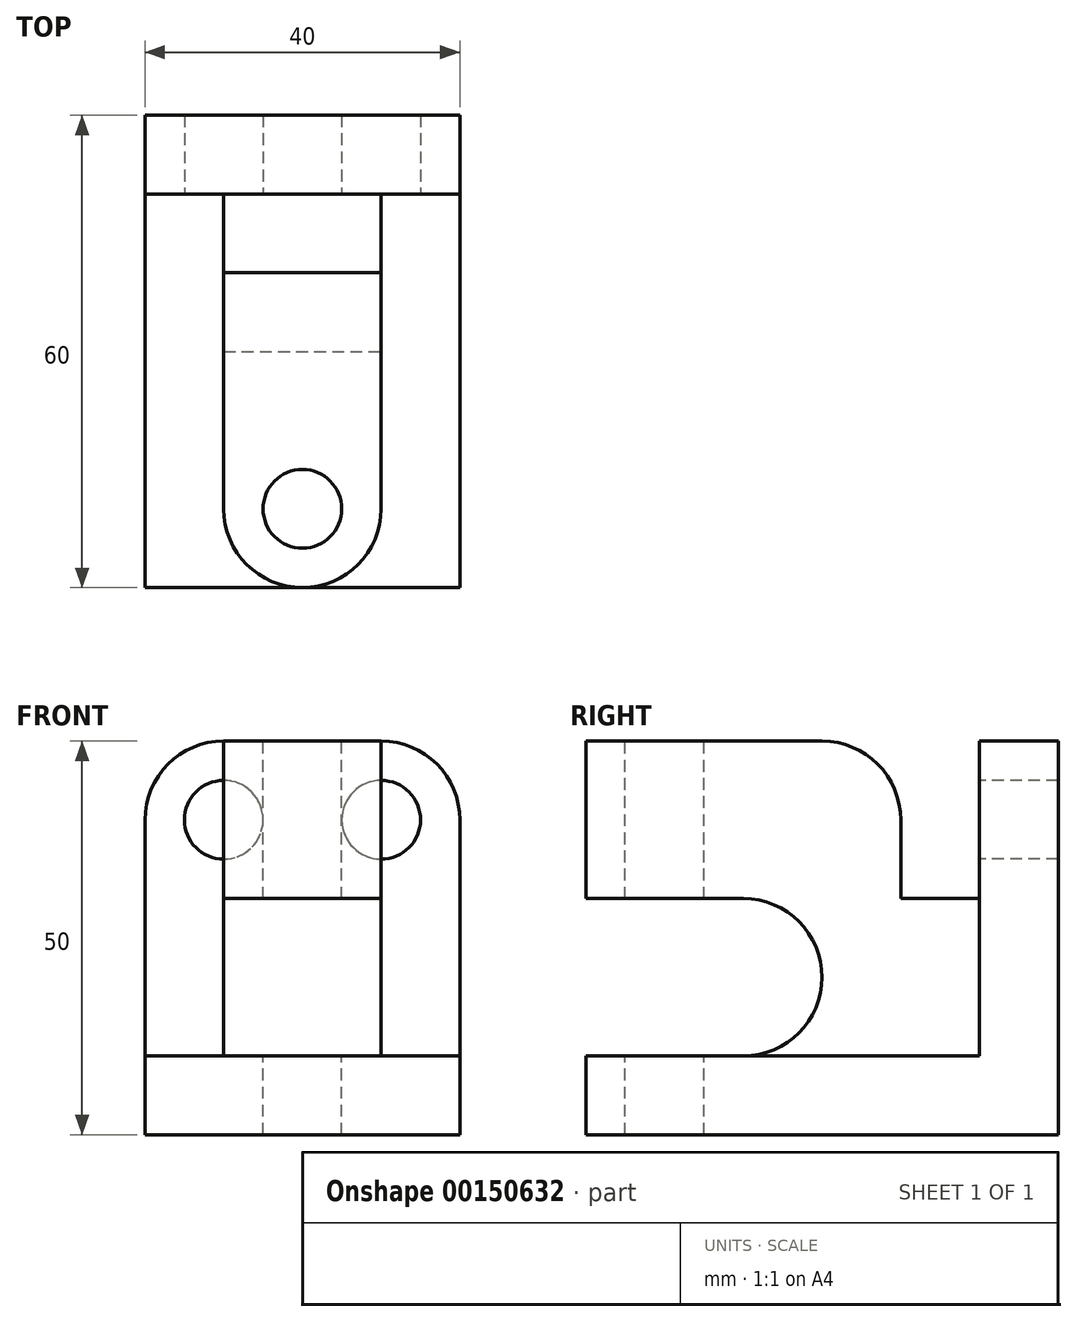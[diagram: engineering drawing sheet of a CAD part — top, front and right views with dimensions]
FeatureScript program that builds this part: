
annotation { "Feature Type Name" : "Feature", "Feature Type Description" : "" }
export const myFeature = defineFeature(function(context is Context, id is Id, definition is map)
    precondition{}
    {
        {
            var Q0;
            Q0=qCreatedBy(makeId("Right.planeOp"),FACE);
            var sketch = newSketch(context, id + "F0", { "sketchPlane" : qUnion([Q0])});
            skLineSegment(sketch, "E0", {"start": v(0, 0) * mm, "end": v(0, 50) * mm});
            skLineSegment(sketch, "E1", {"start": v(0, 50) * mm, "end": v(-10, 50) * mm});
            skLineSegment(sketch, "E2", {"start": v(-10, 50) * mm, "end": v(-10, 10) * mm});
            skLineSegment(sketch, "E3", {"start": v(-10, 10) * mm, "end": v(-60, 10) * mm});
            skLineSegment(sketch, "E4", {"start": v(-60, 10) * mm, "end": v(-60, 0) * mm});
            skLineSegment(sketch, "E5", {"start": v(-60, 0) * mm, "end": v(0, 0) * mm});
            skSolve(sketch);
        }
        {
            var Q0;
            Q0=makeQuery(id+"F0.imprint","IMPRINT",FACE,{"disambiguationData":[TD([[makeQuery(id+"F0.imprint","IMPRINT",EDGE,{"derivedFrom":sQuery(id+"F0.wireOp",EDGE,"E0")}),1.0]])]});
            extrude(context, id + "F1", {"entities" : qUnion([Q0]), "endBound" : BoundingType.SYMMETRIC, "depth" : 40 * mm});
        }
        {
            var Q0;
            Q0=qCreatedBy(makeId("Right.planeOp"),FACE);
            var sketch = newSketch(context, id + "F2", { "sketchPlane" : qUnion([Q0])});
            skLineSegment(sketch, "E6", {"start": v(-10, 10) * mm, "end": v(-60, 10) * mm});
            skLineSegment(sketch, "E7", {"start": v(-60, 10) * mm, "end": v(-60, 50) * mm});
            skLineSegment(sketch, "E8", {"start": v(-60, 50) * mm, "end": v(-30, 50) * mm});
            skLineSegment(sketch, "E9", {"start": v(-20, 40) * mm, "end": v(-20, 30) * mm});
            skLineSegment(sketch, "E10", {"start": v(-20, 30) * mm, "end": v(-10, 30) * mm});
            skLineSegment(sketch, "E11", {"start": v(-10, 30) * mm, "end": v(-10, 10) * mm});
            skPoint(sketch, "E12.visualSharp", {"position": v(-20, 50) * mm});
            skArc(sketch, "E12.filletArc", {"start": v(-20, 40) * mm, "mid": v(-22.93, 47.07) * mm, "end": v(-30, 50) * mm});
            skSolve(sketch);
        }
        {
            var Q0;
            Q0=makeQuery(id+"F2.imprint","IMPRINT",FACE,{"disambiguationData":[TD([[makeQuery(id+"F2.imprint","IMPRINT",EDGE,{"derivedFrom":sQuery(id+"F2.wireOp",EDGE,"E6")}),-1.0]])]});
            extrude(context, id + "F3", {"entities" : qUnion([Q0]), "operationType" : NewBodyOperationType.ADD, "endBound" : BoundingType.SYMMETRIC, "depth" : 20 * mm});
        }
        {
            var Q0;
            Q0=makeQuery(id+"F3.opExtrude","CAP_FACE",FACE,{"disambiguationData":[OSD([sQuery(id+"F2.wireOp",EDGE,"E6"),sQuery(id+"F2.wireOp",EDGE,"E7"),sQuery(id+"F2.wireOp",EDGE,"E8"),sQuery(id+"F2.wireOp",EDGE,"E9"),sQuery(id+"F2.wireOp",EDGE,"E10"),sQuery(id+"F2.wireOp",EDGE,"E11"),sQuery(id+"F2.wireOp",EDGE,"E12.filletArc")])],"isStart":false});
            var sketch = newSketch(context, id + "F4", { "sketchPlane" : qUnion([Q0])});
            skLineSegment(sketch, "E13.bottom", {"start": v(-60, 10) * mm, "end": v(-40, 10) * mm});
            skLineSegment(sketch, "E13.top", {"start": v(-60, 30) * mm, "end": v(-40, 30) * mm});
            skLineSegment(sketch, "E13.left", {"start": v(-60, 10) * mm, "end": v(-60, 30) * mm});
            skArc(sketch, "E14", {"start": v(-40, 10) * mm, "mid": v(-30, 20) * mm, "end": v(-40, 30) * mm});
            skSolve(sketch);
        }
        {
            var Q0;
            Q0=makeQuery(id+"F4.imprint","IMPRINT",FACE,{"disambiguationData":[TD([[makeQuery(id+"F4.imprint","IMPRINT",EDGE,{"derivedFrom":sQuery(id+"F4.wireOp",EDGE,"E13.bottom")}),-1.0]])]});
            extrude(context, id + "F5", {"entities" : qUnion([Q0]), "operationType" : NewBodyOperationType.REMOVE, "endBound" : BoundingType.UP_TO_NEXT, "oppositeDirection" : true, "depth" : 25 * mm});
        }
        {
            var Q0;
            Q0=makeQuery(id+"F1.opExtrude","CAP_EDGE",EDGE,{"disambiguationData":[OSD([sQuery(id+"F0.wireOp",EDGE,"E1")])],"isStart":true});
            var Q1;
            Q1=makeQuery(id+"F1.opExtrude","CAP_EDGE",EDGE,{"disambiguationData":[OSD([sQuery(id+"F0.wireOp",EDGE,"E1")])],"isStart":false});
            var Q2;
            Q2=makeQuery(id+"F3.opExtrude","CAP_EDGE",EDGE,{"disambiguationData":[OSD([sQuery(id+"F2.wireOp",EDGE,"E7")])],"isStart":true});
            var Q3;
            Q3=makeQuery(id+"F3.opExtrude","CAP_EDGE",EDGE,{"disambiguationData":[OSD([sQuery(id+"F2.wireOp",EDGE,"E7")])],"isStart":false});
            var Q4;
            Q4=makeQuery(id+"F3.opExtrude","CAP_EDGE",EDGE,{"disambiguationData":[OSD([sQuery(id+"F2.wireOp",EDGE,"E11")])],"isStart":false});
            var Q5;
            Q5=makeQuery(id+"F3.opExtrude","CAP_EDGE",EDGE,{"disambiguationData":[OSD([sQuery(id+"F2.wireOp",EDGE,"E11")])],"isStart":true});
            fillet(context, id + "F6", {"entities" : qUnion([Q0, Q1, Q2, Q3, Q4, Q5]), "radius" : 10 * mm, "tangentPropagation" : true, "allowEdgeOverflow" : false});
        }
        {
            var Q0;
            Q0=makeQuery(id+"F3.opExtrude","SWEPT_FACE",FACE,{"disambiguationData":[OSD([sQuery(id+"F2.wireOp",EDGE,"E8")])]});
            var sketch = newSketch(context, id + "F7", { "sketchPlane" : qUnion([Q0])});
            skCircle(sketch, "E15", {"center": v(0, -50) * mm, "radius": 5 * mm});
            skSolve(sketch);
        }
        {
            var Q0;
            Q0=sQuery(id+"F7.wireOp",VERTEX,"E15.center");
            var Q1;
            Q1=makeQuery(id+"F1.opExtrude","SWEPT_BODY",BODY,{"disambiguationData":[OSD([sQuery(id+"F0.wireOp",EDGE,"E0"),sQuery(id+"F0.wireOp",EDGE,"E1"),sQuery(id+"F0.wireOp",EDGE,"E2"),sQuery(id+"F0.wireOp",EDGE,"E3"),sQuery(id+"F0.wireOp",EDGE,"E4"),sQuery(id+"F0.wireOp",EDGE,"E5")])]});
            hole(context, id + "F8", {"style" : HoleStyle.SIMPLE, "endStyle" : HoleEndStyle.THROUGH, "holeDiameter" : 10 * mm, "locations" : qUnion([Q0]), "scope" : qUnion([Q1]), "isTappedThrough" : true});
        }
        {
            var Q0;
            Q0=makeQuery(id+"F1.opExtrude","SWEPT_FACE",FACE,{"disambiguationData":[OSD([sQuery(id+"F0.wireOp",EDGE,"E2")])]});
            var sketch = newSketch(context, id + "F9", { "sketchPlane" : qUnion([Q0])});
            skPoint(sketch, "E16", {"position": v(-10, 40) * mm});
            skPoint(sketch, "E17.MirrorP", {"position": v(10, 40) * mm});
            skSolve(sketch);
        }
        {
            var Q0;
            Q0=sQuery(id+"F9.wireOp",VERTEX,"E16");
            var Q1;
            Q1=sQuery(id+"F9.wireOp",VERTEX,"E17.MirrorP");
            var Q2;
            Q2=makeQuery(id+"F1.opExtrude","SWEPT_BODY",BODY,{"disambiguationData":[OSD([sQuery(id+"F0.wireOp",EDGE,"E0"),sQuery(id+"F0.wireOp",EDGE,"E1"),sQuery(id+"F0.wireOp",EDGE,"E2"),sQuery(id+"F0.wireOp",EDGE,"E3"),sQuery(id+"F0.wireOp",EDGE,"E4"),sQuery(id+"F0.wireOp",EDGE,"E5")])]});
            hole(context, id + "F10", {"style" : HoleStyle.SIMPLE, "endStyle" : HoleEndStyle.THROUGH, "holeDiameter" : 10 * mm, "locations" : qUnion([Q0, Q1]), "scope" : qUnion([Q2]), "isTappedThrough" : true});
        }
    });
